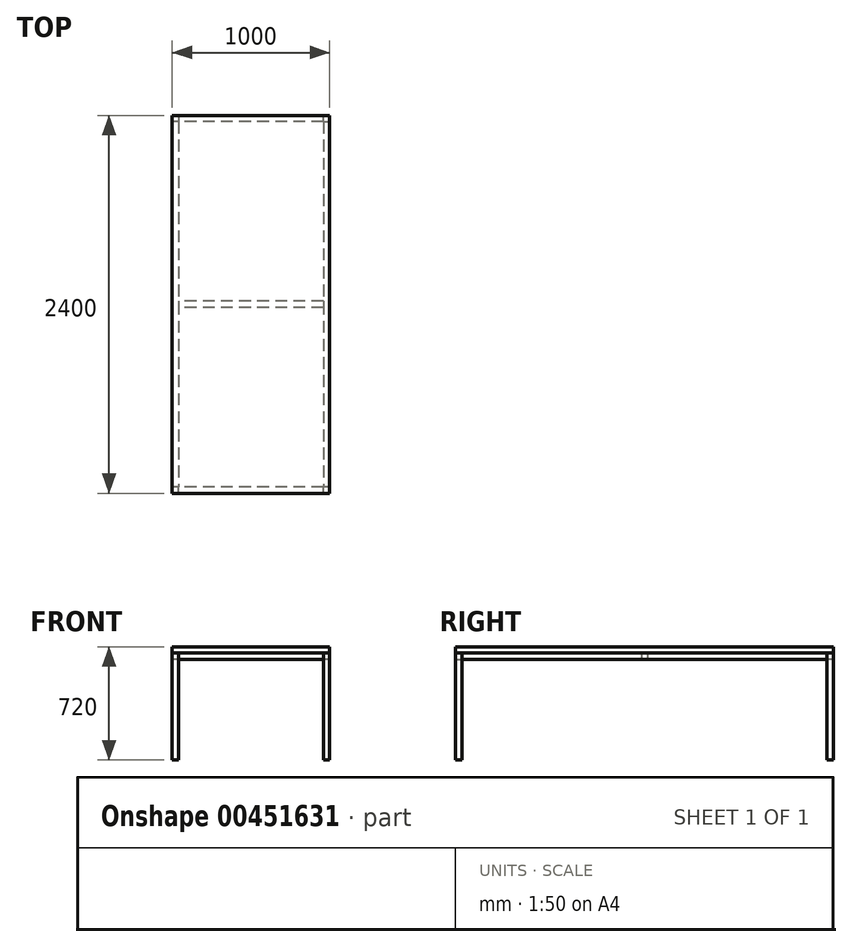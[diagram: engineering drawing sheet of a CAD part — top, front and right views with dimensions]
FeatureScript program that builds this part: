
annotation { "Feature Type Name" : "Feature", "Feature Type Description" : "" }
export const myFeature = defineFeature(function(context is Context, id is Id, definition is map)
    precondition{}
    {
        {
            var Q0;
            Q0=qCreatedBy(makeId("Top.planeOp"),FACE);
            var sketch = newSketch(context, id + "F0", { "sketchPlane" : qUnion([Q0])});
            skLineSegment(sketch, "E0.bottom", {"start": v(0, 0) * mm, "end": v(40, 0) * mm});
            skLineSegment(sketch, "E0.top", {"start": v(0, 40) * mm, "end": v(40, 40) * mm});
            skLineSegment(sketch, "E0.left", {"start": v(0, 0) * mm, "end": v(0, 40) * mm});
            skLineSegment(sketch, "E0.right", {"start": v(40, 0) * mm, "end": v(40, 40) * mm});
            skLineSegment(sketch, "E1.bottom", {"start": v(960, 0) * mm, "end": v(1000, 0) * mm});
            skLineSegment(sketch, "E1.top", {"start": v(960, 40) * mm, "end": v(1000, 40) * mm});
            skLineSegment(sketch, "E1.left", {"start": v(960, 0) * mm, "end": v(960, 40) * mm});
            skLineSegment(sketch, "E1.right", {"start": v(1000, 0) * mm, "end": v(1000, 40) * mm});
            skLineSegment(sketch, "E2.bottom", {"start": v(0, 2360) * mm, "end": v(40, 2360) * mm});
            skLineSegment(sketch, "E2.top", {"start": v(0, 2400) * mm, "end": v(40, 2400) * mm});
            skLineSegment(sketch, "E2.left", {"start": v(0, 2360) * mm, "end": v(0, 2400) * mm});
            skLineSegment(sketch, "E2.right", {"start": v(40, 2360) * mm, "end": v(40, 2400) * mm});
            skLineSegment(sketch, "E3.bottom", {"start": v(960, 2360) * mm, "end": v(1000, 2360) * mm});
            skLineSegment(sketch, "E3.top", {"start": v(960, 2400) * mm, "end": v(1000, 2400) * mm});
            skLineSegment(sketch, "E3.left", {"start": v(960, 2360) * mm, "end": v(960, 2400) * mm});
            skLineSegment(sketch, "E3.right", {"start": v(1000, 2360) * mm, "end": v(1000, 2400) * mm});
            skSolve(sketch);
        }
        {
            var Q0;
            Q0 = qSketchRegion(id + "F0", true);
            extrude(context, id + "F1", {"entities" : qUnion([Q0]), "depth" : 680 * mm});
        }
        {
            var Q0;
            Q0=makeQuery(id+"F1.opExtrude","SWEPT_FACE",FACE,{"disambiguationData":[OSD([sQuery(id+"F0.wireOp",EDGE,"E0.top")])]});
            var sketch = newSketch(context, id + "F2", { "sketchPlane" : qUnion([Q0])});
            skLineSegment(sketch, "E4.bottom", {"start": v(-40, 680) * mm, "end": v(0, 680) * mm});
            skLineSegment(sketch, "E4.top", {"start": v(-40, 640) * mm, "end": v(0, 640) * mm});
            skLineSegment(sketch, "E4.left", {"start": v(-40, 680) * mm, "end": v(-40, 640) * mm});
            skLineSegment(sketch, "E4.right", {"start": v(0, 680) * mm, "end": v(0, 640) * mm});
            skSolve(sketch);
        }
        {
            var Q0;
            Q0=makeQuery(id+"F1.opExtrude","SWEPT_FACE",FACE,{"disambiguationData":[OSD([sQuery(id+"F0.wireOp",EDGE,"E1.top")])]});
            var sketch = newSketch(context, id + "F3", { "sketchPlane" : qUnion([Q0])});
            skLineSegment(sketch, "E5.bottom", {"start": v(-1000, 680) * mm, "end": v(-960, 680) * mm});
            skLineSegment(sketch, "E5.top", {"start": v(-1000, 640) * mm, "end": v(-960, 640) * mm});
            skLineSegment(sketch, "E5.left", {"start": v(-1000, 680) * mm, "end": v(-1000, 640) * mm});
            skLineSegment(sketch, "E5.right", {"start": v(-960, 680) * mm, "end": v(-960, 640) * mm});
            skSolve(sketch);
        }
        {
            var Q0;
            Q0=makeQuery(id+"F2.imprint","IMPRINT",FACE,{"disambiguationData":[TD([[makeQuery(id+"F2.imprint","IMPRINT",EDGE,{"derivedFrom":sQuery(id+"F2.wireOp",EDGE,"E4.bottom")}),1.0]])]});
            var Q1;
            Q1=makeQuery(id+"F3.imprint","IMPRINT",FACE,{"disambiguationData":[TD([[makeQuery(id+"F3.imprint","IMPRINT",EDGE,{"derivedFrom":sQuery(id+"F3.wireOp",EDGE,"E5.bottom")}),1.0]])]});
            extrude(context, id + "F4", {"entities" : qUnion([Q0, Q1]), "depth" : (2400 - (2 * 40)) * mm});
        }
        {
            var Q0;
            Q0=makeQuery(id+"F1.opExtrude","SWEPT_FACE",FACE,{"disambiguationData":[OSD([sQuery(id+"F0.wireOp",EDGE,"E0.right")])]});
            var sketch = newSketch(context, id + "F5", { "sketchPlane" : qUnion([Q0])});
            skLineSegment(sketch, "E6.bottom", {"start": v(0, 680) * mm, "end": v(40, 680) * mm});
            skLineSegment(sketch, "E6.top", {"start": v(0, 640) * mm, "end": v(40, 640) * mm});
            skLineSegment(sketch, "E6.left", {"start": v(0, 680) * mm, "end": v(0, 640) * mm});
            skLineSegment(sketch, "E6.right", {"start": v(40, 680) * mm, "end": v(40, 640) * mm});
            skSolve(sketch);
        }
        {
            var Q0;
            Q0=makeQuery(id+"F4.opExtrude","SWEPT_FACE",FACE,{"disambiguationData":[OSD([sQuery(id+"F2.wireOp",EDGE,"E4.left")])]});
            var sketch = newSketch(context, id + "F6", { "sketchPlane" : qUnion([Q0])});
            skLineSegment(sketch, "E7.bottom", {"start": v(1220, 680) * mm, "end": v(1180, 680) * mm});
            skLineSegment(sketch, "E7.top", {"start": v(1220, 640) * mm, "end": v(1180, 640) * mm});
            skLineSegment(sketch, "E7.left", {"start": v(1220, 680) * mm, "end": v(1220, 640) * mm});
            skLineSegment(sketch, "E7.right", {"start": v(1180, 680) * mm, "end": v(1180, 640) * mm});
            skPoint(sketch, "E7.middle", {"position": v(1200, 660) * mm});
            skPoint(sketch, "E7.middle.positionSnap0", {"position": v(1200, 640) * mm});
            skPoint(sketch, "E7.middle.positionSnap1", {"position": v(40, 660) * mm});
            skPoint(sketch, "E7.centerSnap0", {"position": v(1200, 640) * mm});
            skPoint(sketch, "E7.centerSnap1", {"position": v(40, 660) * mm});
            skSolve(sketch);
        }
        {
            var Q0;
            Q0=makeQuery(id+"F1.opExtrude","SWEPT_FACE",FACE,{"disambiguationData":[OSD([sQuery(id+"F0.wireOp",EDGE,"E2.right")])]});
            var sketch = newSketch(context, id + "F7", { "sketchPlane" : qUnion([Q0])});
            skLineSegment(sketch, "E8.bottom", {"start": v(2400, 680) * mm, "end": v(2360, 680) * mm});
            skLineSegment(sketch, "E8.top", {"start": v(2400, 640) * mm, "end": v(2360, 640) * mm});
            skLineSegment(sketch, "E8.left", {"start": v(2400, 680) * mm, "end": v(2400, 640) * mm});
            skLineSegment(sketch, "E8.right", {"start": v(2360, 680) * mm, "end": v(2360, 640) * mm});
            skSolve(sketch);
        }
        {
            var Q0;
            Q0 = qSketchRegion(id + "F5", true);
            var Q1;
            Q1 = qSketchRegion(id + "F6", true);
            var Q2;
            Q2 = qSketchRegion(id + "F7", true);
            extrude(context, id + "F8", {"entities" : qUnion([Q0, Q1, Q2]), "depth" : (1000 - (2 * 40)) * mm});
        }
        {
            var Q0;
            Q0=qCreatedBy(makeId("Front.planeOp"),FACE);
            var sketch = newSketch(context, id + "F9", { "sketchPlane" : qUnion([Q0])});
            skLineSegment(sketch, "E9.bottom", {"start": v(0, 680) * mm, "end": v(1000, 680) * mm});
            skLineSegment(sketch, "E9.top", {"start": v(0, 720) * mm, "end": v(1000, 720) * mm});
            skLineSegment(sketch, "E9.left", {"start": v(0, 680) * mm, "end": v(0, 720) * mm});
            skLineSegment(sketch, "E9.right", {"start": v(1000, 680) * mm, "end": v(1000, 720) * mm});
            skSolve(sketch);
        }
        {
            var Q0;
            Q0=makeQuery(id+"F9.imprint","IMPRINT",FACE,{"disambiguationData":[TD([[makeQuery(id+"F9.imprint","IMPRINT",EDGE,{"derivedFrom":sQuery(id+"F9.wireOp",EDGE,"E9.bottom")}),1.0]])]});
            extrude(context, id + "F10", {"entities" : qUnion([Q0]), "oppositeDirection" : true, "depth" : 2400 * mm});
        }
    });
